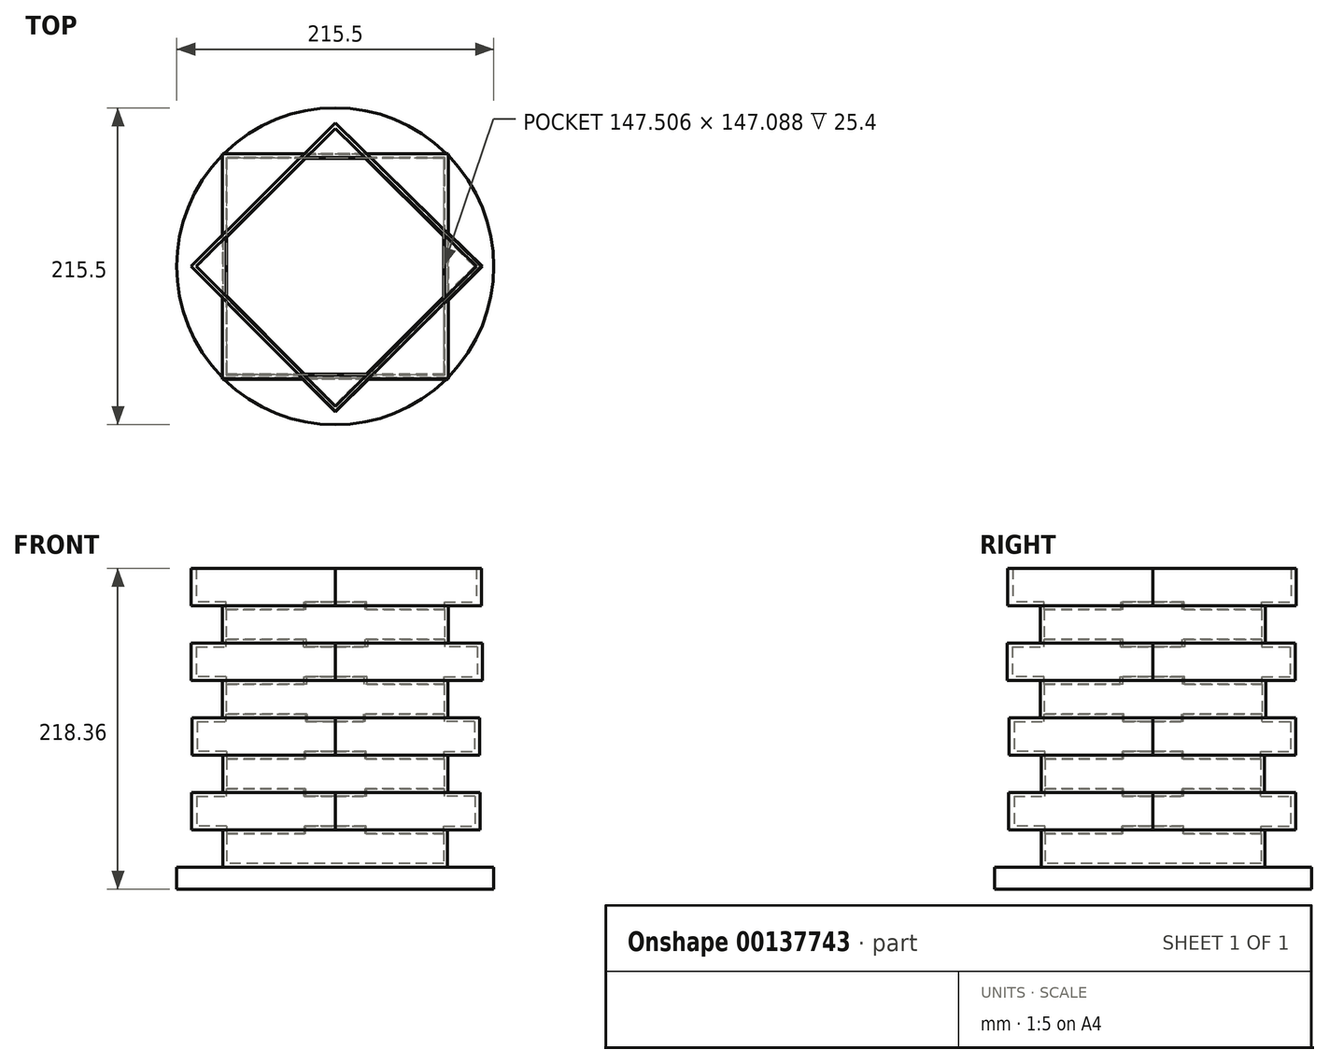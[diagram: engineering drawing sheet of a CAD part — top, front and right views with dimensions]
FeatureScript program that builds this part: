
annotation { "Feature Type Name" : "Feature", "Feature Type Description" : "" }
export const myFeature = defineFeature(function(context is Context, id is Id, definition is map)
    precondition{}
    {
        {
            var Q0;
            Q0=qCreatedBy(makeId("Top.planeOp"),FACE);
            var sketch = newSketch(context, id + "F0", { "sketchPlane" : qUnion([Q0])});
            skLineSegment(sketch, "E0.bottom", {"start": v(76.3, 76.08) * mm, "end": v(-76.3, 76.08) * mm});
            skLineSegment(sketch, "E0.top", {"start": v(76.3, -76.08) * mm, "end": v(-76.3, -76.08) * mm});
            skLineSegment(sketch, "E0.left", {"start": v(76.3, 76.08) * mm, "end": v(76.3, -76.08) * mm});
            skLineSegment(sketch, "E0.right", {"start": v(-76.3, 76.08) * mm, "end": v(-76.3, -76.08) * mm});
            skPoint(sketch, "E0.middle", {"position": v(0, 0) * mm});
            skSolve(sketch);
        }
        {
            var Q0;
            Q0=makeQuery(id+"F0.imprint","IMPRINT",FACE,{"disambiguationData":[TD([[makeQuery(id+"F0.imprint","IMPRINT",EDGE,{"derivedFrom":sQuery(id+"F0.wireOp",EDGE,"E0.bottom")}),1.0]])]});
            extrude(context, id + "F1", {"entities" : qUnion([Q0]), "depth" : 25.4 * mm});
        }
        {
            var Q0;
            Q0=makeQuery(id+"F1.opExtrude","CAP_FACE",FACE,{"disambiguationData":[OSD([sQuery(id+"F0.wireOp",EDGE,"E0.bottom"),sQuery(id+"F0.wireOp",EDGE,"E0.top"),sQuery(id+"F0.wireOp",EDGE,"E0.left"),sQuery(id+"F0.wireOp",EDGE,"E0.right")])],"isStart":false});
            var sketch = newSketch(context, id + "F2", { "sketchPlane" : qUnion([Q0])});
            skLineSegment(sketch, "E1", {"start": v(0, 97.23) * mm, "end": v(-97.65, 0) * mm});
            skPoint(sketch, "E1.startSnap0", {"position": v(0, 76.08) * mm});
            skLineSegment(sketch, "E2", {"start": v(-97.65, 0) * mm, "end": v(0, -98.07) * mm});
            skPoint(sketch, "E2.endSnap0", {"position": v(0, -76.08) * mm});
            skLineSegment(sketch, "E3", {"start": v(0, -98.07) * mm, "end": v(98.5, 0) * mm});
            skPoint(sketch, "E3.endSnap0", {"position": v(76.3, 0) * mm});
            skLineSegment(sketch, "E4", {"start": v(98.5, 0) * mm, "end": v(0, 97.23) * mm});
            skSolve(sketch);
        }
        {
            var Q0;
            {var subQ5=sQuery(id+"F2.wireOp",EDGE,"E1");var subQ13=makeQuery(id+"F1.opExtrude","CAP_EDGE",EDGE,{"disambiguationData":[OSD([sQuery(id+"F0.wireOp",EDGE,"E0.bottom")])],"isStart":false});var subQ15=makeQuery(id+"F2.imprint","INTERSECT",VERTEX,{"derivedFrom":[subQ13,subQ5]});Q0=makeQuery(id+"F2.imprint","IMPRINT",FACE,{"disambiguationData":[TD([[makeQuery(id+"F2.imprint","IMPRINT",EDGE,{"disambiguationData":[TD([[subQ15,-1.0]])],"derivedFrom":subQ5}),1.0]])]});}
            var Q1;
            {var subQ0=sQuery(id+"F2.wireOp",EDGE,"E4");var subQ1=sQuery(id+"F2.wireOp",EDGE,"E3");var subQ2=makeQuery(id+"F2.imprint","INTERSECT",VERTEX,{"derivedFrom":[subQ1,subQ0]});Q1=makeQuery(id+"F2.imprint","IMPRINT",FACE,{"disambiguationData":[TD([[makeQuery(id+"F2.imprint","IMPRINT",EDGE,{"disambiguationData":[TD([[subQ2,1.0]])],"derivedFrom":subQ1}),1.0]])]});}
            var Q2;
            {var subQ0=sQuery(id+"F2.wireOp",EDGE,"E4");var subQ1=sQuery(id+"F2.wireOp",EDGE,"E1");var subQ2=makeQuery(id+"F2.imprint","INTERSECT",VERTEX,{"derivedFrom":[subQ1,subQ0]});Q2=makeQuery(id+"F2.imprint","IMPRINT",FACE,{"disambiguationData":[TD([[makeQuery(id+"F2.imprint","IMPRINT",EDGE,{"disambiguationData":[TD([[subQ2,-1.0]])],"derivedFrom":subQ1}),1.0]])]});}
            var Q3;
            {var subQ0=sQuery(id+"F2.wireOp",EDGE,"E2");var subQ1=sQuery(id+"F2.wireOp",EDGE,"E1");var subQ2=makeQuery(id+"F2.imprint","INTERSECT",VERTEX,{"derivedFrom":[subQ1,subQ0]});Q3=makeQuery(id+"F2.imprint","IMPRINT",FACE,{"disambiguationData":[TD([[makeQuery(id+"F2.imprint","IMPRINT",EDGE,{"disambiguationData":[TD([[subQ2,1.0]])],"derivedFrom":subQ1}),1.0]])]});}
            var Q4;
            {var subQ0=sQuery(id+"F2.wireOp",EDGE,"E3");var subQ1=sQuery(id+"F2.wireOp",EDGE,"E2");var subQ2=makeQuery(id+"F2.imprint","INTERSECT",VERTEX,{"derivedFrom":[subQ1,subQ0]});Q4=makeQuery(id+"F2.imprint","IMPRINT",FACE,{"disambiguationData":[TD([[makeQuery(id+"F2.imprint","IMPRINT",EDGE,{"disambiguationData":[TD([[subQ2,1.0]])],"derivedFrom":subQ1}),1.0]])]});}
            extrude(context, id + "F3", {"entities" : qUnion([Q0, Q1, Q2, Q3, Q4]), "operationType" : NewBodyOperationType.ADD, "depth" : 25.4 * mm});
        }
        {
            var Q0;
            Q0=makeQuery(id+"F3.opExtrude","CAP_FACE",FACE,{"disambiguationData":[OSD([sQuery(id+"F2.wireOp",EDGE,"E1"),sQuery(id+"F2.wireOp",EDGE,"E2"),sQuery(id+"F2.wireOp",EDGE,"E3"),sQuery(id+"F2.wireOp",EDGE,"E4")])],"isStart":false});
            var sketch = newSketch(context, id + "F4", { "sketchPlane" : qUnion([Q0])});
            skLineSegment(sketch, "E5.bottom", {"start": v(76.53, 75.9) * mm, "end": v(-76.53, 75.9) * mm});
            skLineSegment(sketch, "E5.top", {"start": v(76.53, -75.9) * mm, "end": v(-76.53, -75.9) * mm});
            skLineSegment(sketch, "E5.left", {"start": v(76.53, 75.9) * mm, "end": v(76.53, -75.9) * mm});
            skLineSegment(sketch, "E5.right", {"start": v(-76.53, 75.9) * mm, "end": v(-76.53, -75.9) * mm});
            skPoint(sketch, "E5.middle", {"position": v(0, 0) * mm});
            skSolve(sketch);
        }
        {
            var Q0;
            {var subQ9=sQuery(id+"F4.wireOp",EDGE,"E5.bottom");var subQ10=makeQuery(id+"F3.opExtrude","CAP_EDGE",EDGE,{"disambiguationData":[OSD([sQuery(id+"F2.wireOp",EDGE,"E4")])],"isStart":false});var subQ11=makeQuery(id+"F4.imprint","INTERSECT",VERTEX,{"derivedFrom":[subQ10,subQ9]});Q0=makeQuery(id+"F4.imprint","IMPRINT",FACE,{"disambiguationData":[TD([[makeQuery(id+"F4.imprint","IMPRINT",EDGE,{"disambiguationData":[TD([[subQ11,-1.0]])],"derivedFrom":subQ9}),1.0]])]});}
            var Q1;
            {var subQ0=sQuery(id+"F4.wireOp",EDGE,"E5.left");var subQ1=sQuery(id+"F4.wireOp",EDGE,"E5.top");var subQ2=makeQuery(id+"F4.imprint","INTERSECT",VERTEX,{"derivedFrom":[subQ1,subQ0]});Q1=makeQuery(id+"F4.imprint","IMPRINT",FACE,{"disambiguationData":[TD([[makeQuery(id+"F4.imprint","IMPRINT",EDGE,{"disambiguationData":[TD([[subQ2,-1.0]])],"derivedFrom":subQ1}),-1.0]])]});}
            var Q2;
            {var subQ0=sQuery(id+"F4.wireOp",EDGE,"E5.right");var subQ1=sQuery(id+"F4.wireOp",EDGE,"E5.top");var subQ2=makeQuery(id+"F4.imprint","INTERSECT",VERTEX,{"derivedFrom":[subQ1,subQ0]});Q2=makeQuery(id+"F4.imprint","IMPRINT",FACE,{"disambiguationData":[TD([[makeQuery(id+"F4.imprint","IMPRINT",EDGE,{"disambiguationData":[TD([[subQ2,1.0]])],"derivedFrom":subQ1}),-1.0]])]});}
            var Q3;
            {var subQ0=sQuery(id+"F4.wireOp",EDGE,"E5.left");var subQ1=sQuery(id+"F4.wireOp",EDGE,"E5.bottom");var subQ2=makeQuery(id+"F4.imprint","INTERSECT",VERTEX,{"derivedFrom":[subQ1,subQ0]});Q3=makeQuery(id+"F4.imprint","IMPRINT",FACE,{"disambiguationData":[TD([[makeQuery(id+"F4.imprint","IMPRINT",EDGE,{"disambiguationData":[TD([[subQ2,-1.0]])],"derivedFrom":subQ1}),1.0]])]});}
            var Q4;
            {var subQ0=sQuery(id+"F4.wireOp",EDGE,"E5.right");var subQ1=sQuery(id+"F4.wireOp",EDGE,"E5.bottom");var subQ2=makeQuery(id+"F4.imprint","INTERSECT",VERTEX,{"derivedFrom":[subQ1,subQ0]});Q4=makeQuery(id+"F4.imprint","IMPRINT",FACE,{"disambiguationData":[TD([[makeQuery(id+"F4.imprint","IMPRINT",EDGE,{"disambiguationData":[TD([[subQ2,1.0]])],"derivedFrom":subQ1}),1.0]])]});}
            extrude(context, id + "F5", {"entities" : qUnion([Q0, Q1, Q2, Q3, Q4]), "operationType" : NewBodyOperationType.ADD, "depth" : 25.4 * mm});
        }
        {
            var Q0;
            Q0=makeQuery(id+"F5.opExtrude","CAP_FACE",FACE,{"disambiguationData":[OSD([sQuery(id+"F4.wireOp",EDGE,"E5.bottom"),sQuery(id+"F4.wireOp",EDGE,"E5.top"),sQuery(id+"F4.wireOp",EDGE,"E5.left"),sQuery(id+"F4.wireOp",EDGE,"E5.right")])],"isStart":false});
            var sketch = newSketch(context, id + "F6", { "sketchPlane" : qUnion([Q0])});
            skLineSegment(sketch, "E6", {"start": v(0, 97.03) * mm, "end": v(-97.44, 0) * mm});
            skLineSegment(sketch, "E7", {"start": v(-97.44, 0) * mm, "end": v(0, -97.86) * mm});
            skPoint(sketch, "E7.endSnap0", {"position": v(0, -75.9) * mm});
            skLineSegment(sketch, "E8", {"start": v(0, -97.86) * mm, "end": v(98.29, 0) * mm});
            skLineSegment(sketch, "E9", {"start": v(98.29, 0) * mm, "end": v(0, 97.03) * mm});
            skSolve(sketch);
        }
        {
            var Q0;
            {var subQ9=makeQuery(id+"F5.opExtrude","CAP_EDGE",EDGE,{"disambiguationData":[OSD([sQuery(id+"F4.wireOp",EDGE,"E5.bottom")])],"isStart":false});var subQ11=sQuery(id+"F6.wireOp",EDGE,"E6");var subQ12=makeQuery(id+"F6.imprint","INTERSECT",VERTEX,{"derivedFrom":[subQ9,subQ11]});Q0=makeQuery(id+"F6.imprint","IMPRINT",FACE,{"disambiguationData":[TD([[makeQuery(id+"F6.imprint","IMPRINT",EDGE,{"disambiguationData":[TD([[subQ12,-1.0]])],"derivedFrom":subQ11}),1.0]])]});}
            var Q1;
            {var subQ0=sQuery(id+"F6.wireOp",EDGE,"E8");var subQ1=sQuery(id+"F6.wireOp",EDGE,"E7");var subQ2=makeQuery(id+"F6.imprint","INTERSECT",VERTEX,{"derivedFrom":[subQ1,subQ0]});Q1=makeQuery(id+"F6.imprint","IMPRINT",FACE,{"disambiguationData":[TD([[makeQuery(id+"F6.imprint","IMPRINT",EDGE,{"disambiguationData":[TD([[subQ2,1.0]])],"derivedFrom":subQ1}),1.0]])]});}
            var Q2;
            {var subQ0=sQuery(id+"F6.wireOp",EDGE,"E9");var subQ1=sQuery(id+"F6.wireOp",EDGE,"E8");var subQ2=makeQuery(id+"F6.imprint","INTERSECT",VERTEX,{"derivedFrom":[subQ1,subQ0]});Q2=makeQuery(id+"F6.imprint","IMPRINT",FACE,{"disambiguationData":[TD([[makeQuery(id+"F6.imprint","IMPRINT",EDGE,{"disambiguationData":[TD([[subQ2,1.0]])],"derivedFrom":subQ1}),1.0]])]});}
            var Q3;
            {var subQ0=sQuery(id+"F6.wireOp",EDGE,"E7");var subQ1=sQuery(id+"F6.wireOp",EDGE,"E6");var subQ2=makeQuery(id+"F6.imprint","INTERSECT",VERTEX,{"derivedFrom":[subQ1,subQ0]});Q3=makeQuery(id+"F6.imprint","IMPRINT",FACE,{"disambiguationData":[TD([[makeQuery(id+"F6.imprint","IMPRINT",EDGE,{"disambiguationData":[TD([[subQ2,1.0]])],"derivedFrom":subQ1}),1.0]])]});}
            var Q4;
            {var subQ0=sQuery(id+"F6.wireOp",EDGE,"E9");var subQ1=sQuery(id+"F6.wireOp",EDGE,"E6");var subQ2=makeQuery(id+"F6.imprint","INTERSECT",VERTEX,{"derivedFrom":[subQ1,subQ0]});Q4=makeQuery(id+"F6.imprint","IMPRINT",FACE,{"disambiguationData":[TD([[makeQuery(id+"F6.imprint","IMPRINT",EDGE,{"disambiguationData":[TD([[subQ2,-1.0]])],"derivedFrom":subQ1}),1.0]])]});}
            extrude(context, id + "F7", {"entities" : qUnion([Q0, Q1, Q2, Q3, Q4]), "operationType" : NewBodyOperationType.ADD, "depth" : 25.4 * mm});
        }
        {
            var Q0;
            Q0=makeQuery(id+"F7.opExtrude","CAP_FACE",FACE,{"disambiguationData":[OSD([sQuery(id+"F6.wireOp",EDGE,"E6"),sQuery(id+"F6.wireOp",EDGE,"E7"),sQuery(id+"F6.wireOp",EDGE,"E8"),sQuery(id+"F6.wireOp",EDGE,"E9")])],"isStart":false});
            var sketch = newSketch(context, id + "F8", { "sketchPlane" : qUnion([Q0])});
            skLineSegment(sketch, "E10.bottom", {"start": v(76.75, 76.7) * mm, "end": v(-76.75, 76.7) * mm});
            skLineSegment(sketch, "E10.top", {"start": v(76.75, -76.7) * mm, "end": v(-76.75, -76.7) * mm});
            skLineSegment(sketch, "E10.left", {"start": v(76.75, 76.7) * mm, "end": v(76.75, -76.7) * mm});
            skLineSegment(sketch, "E10.right", {"start": v(-76.75, 76.7) * mm, "end": v(-76.75, -76.7) * mm});
            skPoint(sketch, "E10.middle", {"position": v(0, 0) * mm});
            skSolve(sketch);
        }
        {
            var Q0;
            {var subQ1=makeQuery(id+"F7.opExtrude","CAP_EDGE",EDGE,{"disambiguationData":[OSD([sQuery(id+"F6.wireOp",EDGE,"E9")])],"isStart":false});var subQ13=sQuery(id+"F8.wireOp",EDGE,"E10.bottom");var subQ14=makeQuery(id+"F8.imprint","INTERSECT",VERTEX,{"derivedFrom":[subQ1,subQ13]});Q0=makeQuery(id+"F8.imprint","IMPRINT",FACE,{"disambiguationData":[TD([[makeQuery(id+"F8.imprint","IMPRINT",EDGE,{"disambiguationData":[TD([[subQ14,-1.0]])],"derivedFrom":subQ13}),1.0]])]});}
            var Q1;
            {var subQ0=sQuery(id+"F8.wireOp",EDGE,"E10.right");var subQ1=sQuery(id+"F8.wireOp",EDGE,"E10.top");var subQ2=makeQuery(id+"F8.imprint","INTERSECT",VERTEX,{"derivedFrom":[subQ1,subQ0]});Q1=makeQuery(id+"F8.imprint","IMPRINT",FACE,{"disambiguationData":[TD([[makeQuery(id+"F8.imprint","IMPRINT",EDGE,{"disambiguationData":[TD([[subQ2,1.0]])],"derivedFrom":subQ1}),-1.0]])]});}
            var Q2;
            {var subQ0=sQuery(id+"F8.wireOp",EDGE,"E10.left");var subQ1=sQuery(id+"F8.wireOp",EDGE,"E10.top");var subQ2=makeQuery(id+"F8.imprint","INTERSECT",VERTEX,{"derivedFrom":[subQ1,subQ0]});Q2=makeQuery(id+"F8.imprint","IMPRINT",FACE,{"disambiguationData":[TD([[makeQuery(id+"F8.imprint","IMPRINT",EDGE,{"disambiguationData":[TD([[subQ2,-1.0]])],"derivedFrom":subQ1}),-1.0]])]});}
            var Q3;
            {var subQ0=sQuery(id+"F8.wireOp",EDGE,"E10.left");var subQ1=sQuery(id+"F8.wireOp",EDGE,"E10.bottom");var subQ2=makeQuery(id+"F8.imprint","INTERSECT",VERTEX,{"derivedFrom":[subQ1,subQ0]});Q3=makeQuery(id+"F8.imprint","IMPRINT",FACE,{"disambiguationData":[TD([[makeQuery(id+"F8.imprint","IMPRINT",EDGE,{"disambiguationData":[TD([[subQ2,-1.0]])],"derivedFrom":subQ1}),1.0]])]});}
            var Q4;
            {var subQ0=sQuery(id+"F8.wireOp",EDGE,"E10.right");var subQ1=sQuery(id+"F8.wireOp",EDGE,"E10.bottom");var subQ2=makeQuery(id+"F8.imprint","INTERSECT",VERTEX,{"derivedFrom":[subQ1,subQ0]});Q4=makeQuery(id+"F8.imprint","IMPRINT",FACE,{"disambiguationData":[TD([[makeQuery(id+"F8.imprint","IMPRINT",EDGE,{"disambiguationData":[TD([[subQ2,1.0]])],"derivedFrom":subQ1}),1.0]])]});}
            extrude(context, id + "F9", {"entities" : qUnion([Q0, Q1, Q2, Q3, Q4]), "operationType" : NewBodyOperationType.ADD, "depth" : 25.4 * mm});
        }
        {
            var Q0;
            Q0=makeQuery(id+"F9.opExtrude","CAP_FACE",FACE,{"disambiguationData":[OSD([sQuery(id+"F8.wireOp",EDGE,"E10.bottom"),sQuery(id+"F8.wireOp",EDGE,"E10.top"),sQuery(id+"F8.wireOp",EDGE,"E10.left"),sQuery(id+"F8.wireOp",EDGE,"E10.right")])],"isStart":false});
            var sketch = newSketch(context, id + "F10", { "sketchPlane" : qUnion([Q0])});
            skLineSegment(sketch, "E11", {"start": v(0, 96.92) * mm, "end": v(-98, 0) * mm});
            skLineSegment(sketch, "E12", {"start": v(-98, 0) * mm, "end": v(0, -99.1) * mm});
            skPoint(sketch, "E12.endSnap0", {"position": v(0, -76.7) * mm});
            skLineSegment(sketch, "E13", {"start": v(0, -99.1) * mm, "end": v(100.22, 0) * mm});
            skPoint(sketch, "E13.endSnap0", {"position": v(76.75, 0) * mm});
            skLineSegment(sketch, "E14", {"start": v(100.22, 0) * mm, "end": v(0, 96.92) * mm});
            skSolve(sketch);
        }
        {
            var Q0;
            {var subQ3=makeQuery(id+"F9.opExtrude","CAP_EDGE",EDGE,{"disambiguationData":[OSD([sQuery(id+"F8.wireOp",EDGE,"E10.bottom")])],"isStart":false});var subQ13=sQuery(id+"F10.wireOp",EDGE,"E11");var subQ14=makeQuery(id+"F10.imprint","INTERSECT",VERTEX,{"derivedFrom":[subQ3,subQ13]});Q0=makeQuery(id+"F10.imprint","IMPRINT",FACE,{"disambiguationData":[TD([[makeQuery(id+"F10.imprint","IMPRINT",EDGE,{"disambiguationData":[TD([[subQ14,-1.0]])],"derivedFrom":subQ13}),1.0]])]});}
            var Q1;
            {var subQ0=sQuery(id+"F10.wireOp",EDGE,"E13");var subQ1=sQuery(id+"F10.wireOp",EDGE,"E12");var subQ2=makeQuery(id+"F10.imprint","INTERSECT",VERTEX,{"derivedFrom":[subQ1,subQ0]});Q1=makeQuery(id+"F10.imprint","IMPRINT",FACE,{"disambiguationData":[TD([[makeQuery(id+"F10.imprint","IMPRINT",EDGE,{"disambiguationData":[TD([[subQ2,1.0]])],"derivedFrom":subQ1}),1.0]])]});}
            var Q2;
            {var subQ0=sQuery(id+"F10.wireOp",EDGE,"E14");var subQ1=sQuery(id+"F10.wireOp",EDGE,"E13");var subQ2=makeQuery(id+"F10.imprint","INTERSECT",VERTEX,{"derivedFrom":[subQ1,subQ0]});Q2=makeQuery(id+"F10.imprint","IMPRINT",FACE,{"disambiguationData":[TD([[makeQuery(id+"F10.imprint","IMPRINT",EDGE,{"disambiguationData":[TD([[subQ2,1.0]])],"derivedFrom":subQ1}),1.0]])]});}
            var Q3;
            {var subQ0=sQuery(id+"F10.wireOp",EDGE,"E14");var subQ1=sQuery(id+"F10.wireOp",EDGE,"E11");var subQ2=makeQuery(id+"F10.imprint","INTERSECT",VERTEX,{"derivedFrom":[subQ1,subQ0]});Q3=makeQuery(id+"F10.imprint","IMPRINT",FACE,{"disambiguationData":[TD([[makeQuery(id+"F10.imprint","IMPRINT",EDGE,{"disambiguationData":[TD([[subQ2,-1.0]])],"derivedFrom":subQ1}),1.0]])]});}
            var Q4;
            {var subQ0=sQuery(id+"F10.wireOp",EDGE,"E12");var subQ1=sQuery(id+"F10.wireOp",EDGE,"E11");var subQ2=makeQuery(id+"F10.imprint","INTERSECT",VERTEX,{"derivedFrom":[subQ1,subQ0]});Q4=makeQuery(id+"F10.imprint","IMPRINT",FACE,{"disambiguationData":[TD([[makeQuery(id+"F10.imprint","IMPRINT",EDGE,{"disambiguationData":[TD([[subQ2,1.0]])],"derivedFrom":subQ1}),1.0]])]});}
            extrude(context, id + "F11", {"entities" : qUnion([Q0, Q1, Q2, Q3, Q4]), "operationType" : NewBodyOperationType.ADD, "depth" : 25.4 * mm});
        }
        {
            var Q0;
            Q0=makeQuery(id+"F11.opExtrude","CAP_FACE",FACE,{"disambiguationData":[OSD([sQuery(id+"F10.wireOp",EDGE,"E11"),sQuery(id+"F10.wireOp",EDGE,"E12"),sQuery(id+"F10.wireOp",EDGE,"E13"),sQuery(id+"F10.wireOp",EDGE,"E14")])],"isStart":false});
            var sketch = newSketch(context, id + "F12", { "sketchPlane" : qUnion([Q0])});
            skLineSegment(sketch, "E15.bottom", {"start": v(76.8, 76.47) * mm, "end": v(-76.8, 76.47) * mm});
            skLineSegment(sketch, "E15.top", {"start": v(76.8, -76.47) * mm, "end": v(-76.8, -76.47) * mm});
            skLineSegment(sketch, "E15.left", {"start": v(76.8, 76.47) * mm, "end": v(76.8, -76.47) * mm});
            skLineSegment(sketch, "E15.right", {"start": v(-76.8, 76.47) * mm, "end": v(-76.8, -76.47) * mm});
            skPoint(sketch, "E15.middle", {"position": v(0, 0) * mm});
            skSolve(sketch);
        }
        {
            var Q0;
            {var subQ6=makeQuery(id+"F11.opExtrude","CAP_EDGE",EDGE,{"disambiguationData":[OSD([sQuery(id+"F10.wireOp",EDGE,"E14")])],"isStart":false});var subQ13=sQuery(id+"F12.wireOp",EDGE,"E15.bottom");var subQ15=makeQuery(id+"F12.imprint","INTERSECT",VERTEX,{"derivedFrom":[subQ6,subQ13]});Q0=makeQuery(id+"F12.imprint","IMPRINT",FACE,{"disambiguationData":[TD([[makeQuery(id+"F12.imprint","IMPRINT",EDGE,{"disambiguationData":[TD([[subQ15,-1.0]])],"derivedFrom":subQ13}),1.0]])]});}
            var Q1;
            {var subQ0=sQuery(id+"F12.wireOp",EDGE,"E15.right");var subQ1=sQuery(id+"F12.wireOp",EDGE,"E15.top");var subQ2=makeQuery(id+"F12.imprint","INTERSECT",VERTEX,{"derivedFrom":[subQ1,subQ0]});Q1=makeQuery(id+"F12.imprint","IMPRINT",FACE,{"disambiguationData":[TD([[makeQuery(id+"F12.imprint","IMPRINT",EDGE,{"disambiguationData":[TD([[subQ2,1.0]])],"derivedFrom":subQ1}),-1.0]])]});}
            var Q2;
            {var subQ0=sQuery(id+"F12.wireOp",EDGE,"E15.left");var subQ1=sQuery(id+"F12.wireOp",EDGE,"E15.top");var subQ2=makeQuery(id+"F12.imprint","INTERSECT",VERTEX,{"derivedFrom":[subQ1,subQ0]});Q2=makeQuery(id+"F12.imprint","IMPRINT",FACE,{"disambiguationData":[TD([[makeQuery(id+"F12.imprint","IMPRINT",EDGE,{"disambiguationData":[TD([[subQ2,-1.0]])],"derivedFrom":subQ1}),-1.0]])]});}
            var Q3;
            {var subQ0=sQuery(id+"F12.wireOp",EDGE,"E15.left");var subQ1=sQuery(id+"F12.wireOp",EDGE,"E15.bottom");var subQ2=makeQuery(id+"F12.imprint","INTERSECT",VERTEX,{"derivedFrom":[subQ1,subQ0]});Q3=makeQuery(id+"F12.imprint","IMPRINT",FACE,{"disambiguationData":[TD([[makeQuery(id+"F12.imprint","IMPRINT",EDGE,{"disambiguationData":[TD([[subQ2,-1.0]])],"derivedFrom":subQ1}),1.0]])]});}
            var Q4;
            {var subQ0=sQuery(id+"F12.wireOp",EDGE,"E15.right");var subQ1=sQuery(id+"F12.wireOp",EDGE,"E15.bottom");var subQ2=makeQuery(id+"F12.imprint","INTERSECT",VERTEX,{"derivedFrom":[subQ1,subQ0]});Q4=makeQuery(id+"F12.imprint","IMPRINT",FACE,{"disambiguationData":[TD([[makeQuery(id+"F12.imprint","IMPRINT",EDGE,{"disambiguationData":[TD([[subQ2,1.0]])],"derivedFrom":subQ1}),1.0]])]});}
            extrude(context, id + "F13", {"entities" : qUnion([Q0, Q1, Q2, Q3, Q4]), "operationType" : NewBodyOperationType.ADD, "depth" : 25.4 * mm});
        }
        {
            var Q0;
            Q0=makeQuery(id+"F13.opExtrude","CAP_FACE",FACE,{"disambiguationData":[OSD([sQuery(id+"F12.wireOp",EDGE,"E15.bottom"),sQuery(id+"F12.wireOp",EDGE,"E15.top"),sQuery(id+"F12.wireOp",EDGE,"E15.left"),sQuery(id+"F12.wireOp",EDGE,"E15.right")])],"isStart":false});
            var sketch = newSketch(context, id + "F14", { "sketchPlane" : qUnion([Q0])});
            skLineSegment(sketch, "E16", {"start": v(0, 97.36) * mm, "end": v(-98.09, 0) * mm});
            skPoint(sketch, "E16.startSnap0", {"position": v(0, 76.47) * mm});
            skLineSegment(sketch, "E17", {"start": v(-98.09, 0) * mm, "end": v(0, -98.82) * mm});
            skPoint(sketch, "E17.endSnap0", {"position": v(0, -76.47) * mm});
            skLineSegment(sketch, "E18", {"start": v(0, -98.82) * mm, "end": v(99.56, 0) * mm});
            skLineSegment(sketch, "E19", {"start": v(99.56, 0) * mm, "end": v(0, 97.36) * mm});
            skSolve(sketch);
        }
        {
            var Q0;
            {var subQ11=makeQuery(id+"F13.opExtrude","CAP_EDGE",EDGE,{"disambiguationData":[OSD([sQuery(id+"F12.wireOp",EDGE,"E15.bottom")])],"isStart":false});var subQ13=sQuery(id+"F14.wireOp",EDGE,"E16");var subQ14=makeQuery(id+"F14.imprint","INTERSECT",VERTEX,{"derivedFrom":[subQ11,subQ13]});Q0=makeQuery(id+"F14.imprint","IMPRINT",FACE,{"disambiguationData":[TD([[makeQuery(id+"F14.imprint","IMPRINT",EDGE,{"disambiguationData":[TD([[subQ14,-1.0]])],"derivedFrom":subQ13}),1.0]])]});}
            var Q1;
            {var subQ0=sQuery(id+"F14.wireOp",EDGE,"E17");var subQ1=sQuery(id+"F14.wireOp",EDGE,"E16");var subQ2=makeQuery(id+"F14.imprint","INTERSECT",VERTEX,{"derivedFrom":[subQ1,subQ0]});Q1=makeQuery(id+"F14.imprint","IMPRINT",FACE,{"disambiguationData":[TD([[makeQuery(id+"F14.imprint","IMPRINT",EDGE,{"disambiguationData":[TD([[subQ2,1.0]])],"derivedFrom":subQ1}),1.0]])]});}
            var Q2;
            {var subQ0=sQuery(id+"F14.wireOp",EDGE,"E19");var subQ1=sQuery(id+"F14.wireOp",EDGE,"E16");var subQ2=makeQuery(id+"F14.imprint","INTERSECT",VERTEX,{"derivedFrom":[subQ1,subQ0]});Q2=makeQuery(id+"F14.imprint","IMPRINT",FACE,{"disambiguationData":[TD([[makeQuery(id+"F14.imprint","IMPRINT",EDGE,{"disambiguationData":[TD([[subQ2,-1.0]])],"derivedFrom":subQ1}),1.0]])]});}
            var Q3;
            {var subQ0=sQuery(id+"F14.wireOp",EDGE,"E19");var subQ1=sQuery(id+"F14.wireOp",EDGE,"E18");var subQ2=makeQuery(id+"F14.imprint","INTERSECT",VERTEX,{"derivedFrom":[subQ1,subQ0]});Q3=makeQuery(id+"F14.imprint","IMPRINT",FACE,{"disambiguationData":[TD([[makeQuery(id+"F14.imprint","IMPRINT",EDGE,{"disambiguationData":[TD([[subQ2,1.0]])],"derivedFrom":subQ1}),1.0]])]});}
            var Q4;
            {var subQ0=sQuery(id+"F14.wireOp",EDGE,"E18");var subQ1=sQuery(id+"F14.wireOp",EDGE,"E17");var subQ2=makeQuery(id+"F14.imprint","INTERSECT",VERTEX,{"derivedFrom":[subQ1,subQ0]});Q4=makeQuery(id+"F14.imprint","IMPRINT",FACE,{"disambiguationData":[TD([[makeQuery(id+"F14.imprint","IMPRINT",EDGE,{"disambiguationData":[TD([[subQ2,1.0]])],"derivedFrom":subQ1}),1.0]])]});}
            extrude(context, id + "F15", {"entities" : qUnion([Q0, Q1, Q2, Q3, Q4]), "operationType" : NewBodyOperationType.ADD, "depth" : 25.4 * mm});
        }
        {
            var Q0;
            Q0=makeQuery(id+"F15.opExtrude","CAP_FACE",FACE,{"disambiguationData":[OSD([sQuery(id+"F14.wireOp",EDGE,"E16"),sQuery(id+"F14.wireOp",EDGE,"E17"),sQuery(id+"F14.wireOp",EDGE,"E18"),sQuery(id+"F14.wireOp",EDGE,"E19")])],"isStart":false});
            shell(context, id + "F16", {"entities" : qUnion([Q0]), "thickness" : 2.54 * mm});
        }
        {
            var Q0;
            Q0=makeQuery(id+"F1.opExtrude","CAP_FACE",FACE,{"disambiguationData":[OSD([sQuery(id+"F0.wireOp",EDGE,"E0.bottom"),sQuery(id+"F0.wireOp",EDGE,"E0.top"),sQuery(id+"F0.wireOp",EDGE,"E0.left"),sQuery(id+"F0.wireOp",EDGE,"E0.right")])],"isStart":true});
            var sketch = newSketch(context, id + "F17", { "sketchPlane" : qUnion([Q0])});
            skCircle(sketch, "E20", {"center": v(0, 0) * mm, "radius": 107.75 * mm});
            skSolve(sketch);
        }
        {
            var Q0;
            Q0=makeQuery(id+"F17.imprint","IMPRINT",FACE,{"disambiguationData":[TD([[makeQuery(id+"F17.imprint","IMPRINT",EDGE,{"derivedFrom":makeQuery(id+"F1.opExtrude","CAP_EDGE",EDGE,{"disambiguationData":[OSD([sQuery(id+"F0.wireOp",EDGE,"E0.bottom")])],"isStart":true})}),-1.0]])]});
            var Q1;
            {var subQ1=makeQuery(id+"F1.opExtrude","CAP_EDGE",EDGE,{"disambiguationData":[OSD([sQuery(id+"F0.wireOp",EDGE,"E0.right")])],"isStart":true});Q1=makeQuery(id+"F17.imprint","IMPRINT",FACE,{"disambiguationData":[TD([[makeQuery(id+"F17.imprint","IMPRINT",EDGE,{"derivedFrom":subQ1}),1.0]])]});}
            var Q2;
            {var subQ1=makeQuery(id+"F1.opExtrude","CAP_EDGE",EDGE,{"disambiguationData":[OSD([sQuery(id+"F0.wireOp",EDGE,"E0.top")])],"isStart":true});Q2=makeQuery(id+"F17.imprint","IMPRINT",FACE,{"disambiguationData":[TD([[makeQuery(id+"F17.imprint","IMPRINT",EDGE,{"derivedFrom":subQ1}),-1.0]])]});}
            var Q3;
            {var subQ1=makeQuery(id+"F1.opExtrude","CAP_EDGE",EDGE,{"disambiguationData":[OSD([sQuery(id+"F0.wireOp",EDGE,"E0.left")])],"isStart":true});Q3=makeQuery(id+"F17.imprint","IMPRINT",FACE,{"disambiguationData":[TD([[makeQuery(id+"F17.imprint","IMPRINT",EDGE,{"derivedFrom":subQ1}),-1.0]])]});}
            var Q4;
            {var subQ1=makeQuery(id+"F1.opExtrude","CAP_EDGE",EDGE,{"disambiguationData":[OSD([sQuery(id+"F0.wireOp",EDGE,"E0.bottom")])],"isStart":true});Q4=makeQuery(id+"F17.imprint","IMPRINT",FACE,{"disambiguationData":[TD([[makeQuery(id+"F17.imprint","IMPRINT",EDGE,{"derivedFrom":subQ1}),1.0]])]});}
            extrude(context, id + "F18", {"entities" : qUnion([Q0, Q1, Q2, Q3, Q4]), "operationType" : NewBodyOperationType.ADD, "depth" : 15.16 * mm});
        }
    });
